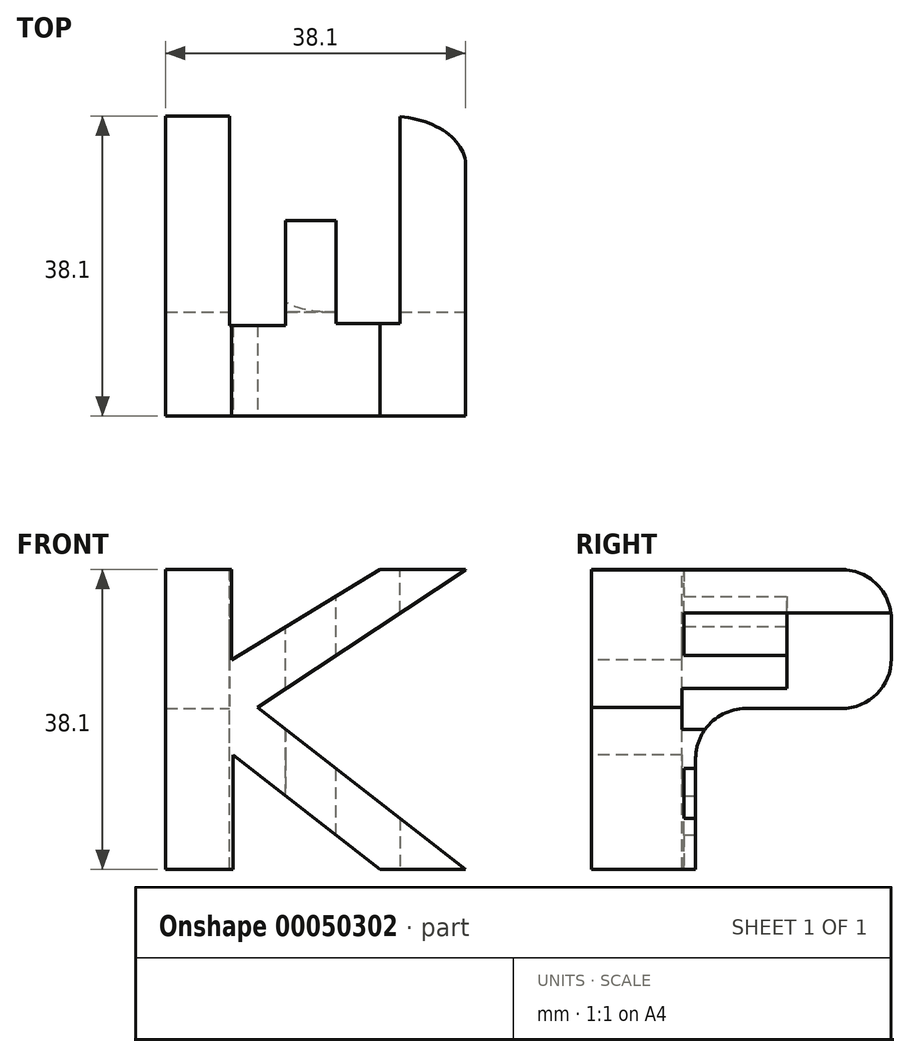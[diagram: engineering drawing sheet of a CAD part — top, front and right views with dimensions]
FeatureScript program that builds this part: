
annotation { "Feature Type Name" : "Feature", "Feature Type Description" : "" }
export const myFeature = defineFeature(function(context is Context, id is Id, definition is map)
    precondition{}
    {
        {
            var Q0;
            Q0=qCreatedBy(makeId("Front.planeOp"),FACE);
            var sketch = newSketch(context, id + "F0", { "sketchPlane" : qUnion([Q0])});
            skLineSegment(sketch, "E0", {"start": v(0, 0) * mm, "end": v(38.1, 0) * mm});
            skLineSegment(sketch, "E1", {"start": v(38.1, 0) * mm, "end": v(38.1, 38.1) * mm});
            skLineSegment(sketch, "E2", {"start": v(38.1, 38.1) * mm, "end": v(0, 38.1) * mm});
            skLineSegment(sketch, "E3", {"start": v(0, 38.1) * mm, "end": v(0, 0) * mm});
            skSolve(sketch);
        }
        {
            var Q0;
            Q0 = qSketchRegion(id + "F0", true);
            extrude(context, id + "F1", {"entities" : qUnion([Q0]), "depth" : 38.1 * mm});
        }
        {
            var Q0;
            Q0=qCreatedBy(makeId("Front.planeOp"),FACE);
            cPlane(context, id + "F2", {"entities" : qUnion([Q0]), "cplaneType" : CPlaneType.OFFSET, "offset" : 38.1 * mm, "width" : 152.4 * mm, "height" : 152.4 * mm});
        }
        {
            var Q0;
            Q0=qCreatedBy(id+"F2.planeOp",FACE);
            var sketch = newSketch(context, id + "F3", { "sketchPlane" : qUnion([Q0])});
            skLineSegment(sketch, "E4", {"start": v(0, 38.1) * mm, "end": v(8.37, 38.1) * mm});
            skLineSegment(sketch, "E5", {"start": v(8.37, 38.1) * mm, "end": v(8.37, 26.58) * mm});
            skLineSegment(sketch, "E6", {"start": v(8.37, 26.58) * mm, "end": v(27.23, 38.1) * mm});
            skLineSegment(sketch, "E7", {"start": v(27.23, 38.1) * mm, "end": v(38.15, 38.1) * mm});
            skLineSegment(sketch, "E8", {"start": v(38.15, 38.1) * mm, "end": v(11.66, 20.6) * mm});
            skLineSegment(sketch, "E9", {"start": v(11.66, 20.6) * mm, "end": v(38.1, 0) * mm});
            skLineSegment(sketch, "E10", {"start": v(38.1, 0) * mm, "end": v(27.23, 0) * mm});
            skLineSegment(sketch, "E11", {"start": v(27.23, 0) * mm, "end": v(8.56, 14.55) * mm});
            skLineSegment(sketch, "E12", {"start": v(8.56, 14.55) * mm, "end": v(8.56, 0) * mm});
            skLineSegment(sketch, "E13", {"start": v(8.56, 0) * mm, "end": v(0, 0) * mm});
            skLineSegment(sketch, "E14", {"start": v(0, 38.1) * mm, "end": v(0, 0) * mm});
            skLineSegment(sketch, "E15", {"start": v(0, 0) * mm, "end": v(0, 38.1) * mm});
            skLineSegment(sketch, "E16", {"start": v(38.15, 38.1) * mm, "end": v(38.1, 0) * mm});
            skLineSegment(sketch, "E17", {"start": v(0, 0) * mm, "end": v(38.1, 0) * mm});
            skLineSegment(sketch, "E18", {"start": v(8.37, 38.1) * mm, "end": v(27.23, 38.1) * mm});
            skLineSegment(sketch, "E19", {"start": v(27.23, 0) * mm, "end": v(8.56, 0) * mm});
            skSolve(sketch);
        }
        {
            var Q0;
            Q0=makeQuery(id+"F3.imprint","IMPRINT",FACE,{"disambiguationData":[TD([[makeQuery(id+"F3.imprint","IMPRINT",EDGE,{"derivedFrom":sQuery(id+"F3.wireOp",EDGE,"E5")}),1.0]])]});
            var Q1;
            Q1=makeQuery(id+"F3.imprint","IMPRINT",FACE,{"disambiguationData":[TD([[makeQuery(id+"F3.imprint","IMPRINT",EDGE,{"derivedFrom":sQuery(id+"F3.wireOp",EDGE,"E8")}),1.0]])]});
            var Q2;
            Q2=makeQuery(id+"F3.imprint","IMPRINT",FACE,{"disambiguationData":[TD([[makeQuery(id+"F3.imprint","IMPRINT",EDGE,{"derivedFrom":sQuery(id+"F3.wireOp",EDGE,"E11")}),1.0]])]});
            extrude(context, id + "F4", {"entities" : qUnion([Q0, Q1, Q2]), "operationType" : NewBodyOperationType.REMOVE, "oppositeDirection" : true, "depth" : 38.1 * mm});
        }
        {
            var Q0;
            Q0=qCreatedBy(makeId("Right.planeOp"),FACE);
            cPlane(context, id + "F5", {"entities" : qUnion([Q0]), "cplaneType" : CPlaneType.OFFSET, "offset" : 38.1 * mm, "width" : 152.4 * mm, "height" : 152.4 * mm});
        }
        {
            var Q0;
            Q0=qCreatedBy(id+"F5.planeOp",FACE);
            var sketch = newSketch(context, id + "F6", { "sketchPlane" : qUnion([Q0])});
            skLineSegment(sketch, "E20", {"start": v(0, 0) * mm, "end": v(0, 38.1) * mm});
            skLineSegment(sketch, "E21", {"start": v(-6.35, 38.1) * mm, "end": v(-38.1, 38.1) * mm});
            skLineSegment(sketch, "E22", {"start": v(-38.1, 38.1) * mm, "end": v(-38.1, 0) * mm});
            skLineSegment(sketch, "E23", {"start": v(-38.1, 0) * mm, "end": v(0, 0) * mm});
            skLineSegment(sketch, "E24", {"start": v(0, 38.1) * mm, "end": v(0, 0) * mm});
            skLineSegment(sketch, "E25", {"start": v(-24.86, 0) * mm, "end": v(-24.86, 14.08) * mm});
            skLineSegment(sketch, "E26", {"start": v(-18.51, 20.43) * mm, "end": v(-6.35, 20.43) * mm});
            skLineSegment(sketch, "E27", {"start": v(0, 26.78) * mm, "end": v(0, 31.75) * mm});
            skPoint(sketch, "E28.visualSharp", {"position": v(0, 38.1) * mm});
            skArc(sketch, "E28.filletArc", {"start": v(0, 31.75) * mm, "mid": v(-1.86, 36.24) * mm, "end": v(-6.35, 38.1) * mm});
            skPoint(sketch, "E29.visualSharp", {"position": v(0, 20.43) * mm});
            skArc(sketch, "E29.filletArc", {"start": v(-6.35, 20.43) * mm, "mid": v(-1.86, 22.3) * mm, "end": v(0, 26.78) * mm});
            skPoint(sketch, "E30.visualSharp", {"position": v(-24.86, 20.43) * mm});
            skArc(sketch, "E30.filletArc", {"start": v(-18.51, 20.43) * mm, "mid": v(-23, 18.57) * mm, "end": v(-24.86, 14.08) * mm});
            skLineSegment(sketch, "E31", {"start": v(0, 38.1) * mm, "end": v(-6.35, 38.1) * mm});
            skSolve(sketch);
        }
        {
            var Q0;
            {var subQ2=sQuery(id+"F6.wireOp",EDGE,"E28.filletArc");Q0=makeQuery(id+"F6.imprint","IMPRINT",FACE,{"disambiguationData":[TD([[makeQuery(id+"F6.imprint","IMPRINT",EDGE,{"derivedFrom":subQ2}),-1.0]])]});}
            var Q1;
            {var subQ0=sQuery(id+"F6.wireOp",EDGE,"E25");Q1=makeQuery(id+"F6.imprint","IMPRINT",FACE,{"disambiguationData":[TD([[makeQuery(id+"F6.imprint","IMPRINT",EDGE,{"derivedFrom":subQ0}),-1.0]])]});}
            extrude(context, id + "F7", {"entities" : qUnion([Q0, Q1]), "operationType" : NewBodyOperationType.REMOVE, "oppositeDirection" : true, "depth" : 38.1 * mm});
        }
        {
            var Q0;
            Q0=qCreatedBy(makeId("Top.planeOp"),FACE);
            cPlane(context, id + "F8", {"entities" : qUnion([Q0]), "cplaneType" : CPlaneType.OFFSET, "offset" : 38.1 * mm, "width" : 152.4 * mm, "height" : 152.4 * mm});
        }
        {
            var Q0;
            Q0=qCreatedBy(id+"F8.planeOp",FACE);
            var sketch = newSketch(context, id + "F9", { "sketchPlane" : qUnion([Q0])});
            skLineSegment(sketch, "E32.bottom", {"start": v(0, 0) * mm, "end": v(38.1, 0) * mm});
            skLineSegment(sketch, "E32.top", {"start": v(0, -38.1) * mm, "end": v(38.1, -38.1) * mm});
            skLineSegment(sketch, "E32.left", {"start": v(0, 0) * mm, "end": v(0, -38.1) * mm});
            skLineSegment(sketch, "E32.right", {"start": v(38.1, 0) * mm, "end": v(38.1, -38.1) * mm});
            skLineSegment(sketch, "E33", {"start": v(0, -38.1) * mm, "end": v(0, 0) * mm});
            skLineSegment(sketch, "E34", {"start": v(8.12, 0) * mm, "end": v(8.12, -26.59) * mm});
            skLineSegment(sketch, "E35", {"start": v(8.12, -26.59) * mm, "end": v(15.26, -26.59) * mm});
            skLineSegment(sketch, "E36", {"start": v(15.26, -26.59) * mm, "end": v(15.26, -13.3) * mm});
            skLineSegment(sketch, "E37", {"start": v(15.26, -13.3) * mm, "end": v(21.66, -13.3) * mm});
            skLineSegment(sketch, "E38", {"start": v(21.66, -13.3) * mm, "end": v(21.66, -26.34) * mm});
            skLineSegment(sketch, "E39", {"start": v(21.66, -26.34) * mm, "end": v(29.79, -26.34) * mm});
            skLineSegment(sketch, "E40", {"start": v(29.79, -26.34) * mm, "end": v(29.79, 0) * mm});
            skSolve(sketch);
        }
        {
            var Q0;
            {var subQ0=sQuery(id+"F9.wireOp",EDGE,"E34");Q0=makeQuery(id+"F9.imprint","IMPRINT",FACE,{"disambiguationData":[TD([[makeQuery(id+"F9.imprint","IMPRINT",EDGE,{"derivedFrom":subQ0}),1.0]])]});}
            extrude(context, id + "F10", {"entities" : qUnion([Q0]), "operationType" : NewBodyOperationType.REMOVE, "oppositeDirection" : true, "depth" : 38.1 * mm});
        }
    });
